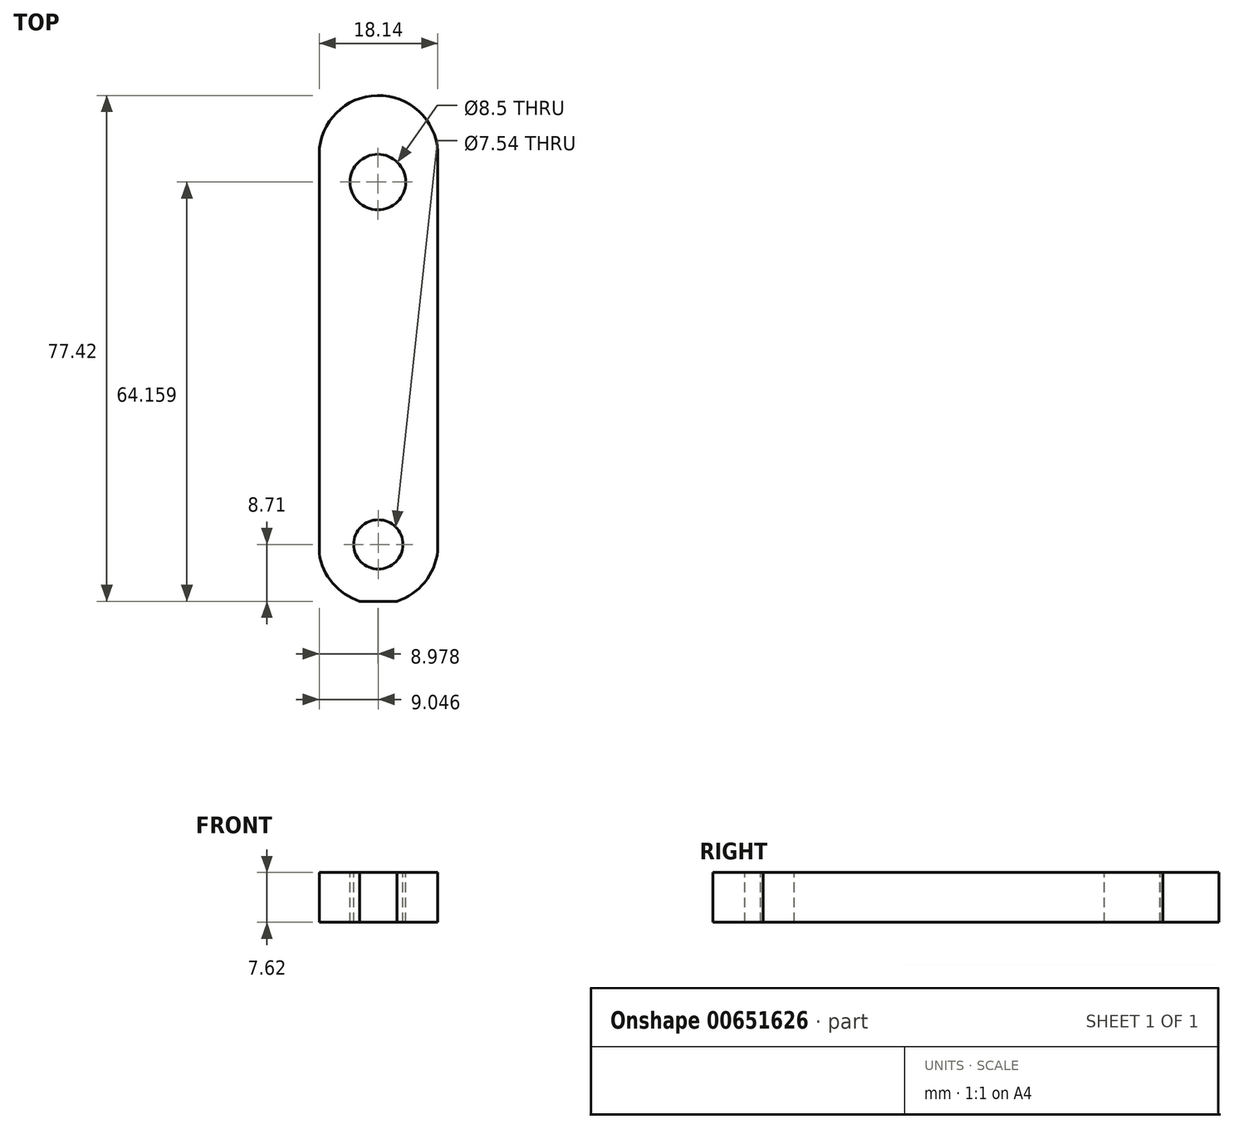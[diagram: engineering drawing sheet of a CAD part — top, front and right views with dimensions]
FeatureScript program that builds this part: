
annotation { "Feature Type Name" : "Feature", "Feature Type Description" : "" }
export const myFeature = defineFeature(function(context is Context, id is Id, definition is map)
    precondition{}
    {
        {
            var Q0;
            Q0=qCreatedBy(makeId("Top.planeOp"),FACE);
            var sketch = newSketch(context, id + "F0", { "sketchPlane" : qUnion([Q0])});
            skLineSegment(sketch, "E0.bottom", {"start": v(-9.26, -43.08) * mm, "end": v(-27.4, -43.08) * mm});
            skLineSegment(sketch, "E0.top", {"start": v(-9.26, 34.64) * mm, "end": v(-27.4, 34.64) * mm});
            skLineSegment(sketch, "E0.left", {"start": v(-9.26, -43.08) * mm, "end": v(-9.26, 34.64) * mm});
            skLineSegment(sketch, "E0.right", {"start": v(-27.4, -43.08) * mm, "end": v(-27.4, 34.64) * mm});
            skSolve(sketch);
        }
        {
            var Q0;
            Q0 = qSketchRegion(id + "F0", true);
            extrude(context, id + "F1", {"entities" : qUnion([Q0]), "depth" : 7.62 * mm, "offsetDistance" : 25.4 * mm});
        }
        {
            var Q0;
            Q0=makeQuery(id+"F1.opExtrude","CAP_FACE",FACE,{"disambiguationData":[OSD([sQuery(id+"F0.wireOp",EDGE,"E0.bottom"),sQuery(id+"F0.wireOp",EDGE,"E0.top"),sQuery(id+"F0.wireOp",EDGE,"E0.left"),sQuery(id+"F0.wireOp",EDGE,"E0.right")])],"isStart":false});
            var sketch = newSketch(context, id + "F2", { "sketchPlane" : qUnion([Q0])});
            skArc(sketch, "E1", {"start": v(-9.26, 24.75) * mm, "mid": v(-18.14, 34.34) * mm, "end": v(-27.4, 25.11) * mm});
            skArc(sketch, "E2", {"start": v(-27.4, -35.74) * mm, "mid": v(-18.17, -43.52) * mm, "end": v(-9.26, -35.38) * mm});
            skSolve(sketch);
        }
        {
            var Q0;
            {var subQ5=makeQuery(id+"F1.opExtrude","CAP_EDGE",EDGE,{"disambiguationData":[OSD([sQuery(id+"F0.wireOp",EDGE,"E0.top")])],"isStart":false});Q0=makeQuery(id+"F2.imprint","IMPRINT",FACE,{"disambiguationData":[TD([[makeQuery(id+"F2.imprint","IMPRINT",EDGE,{"derivedFrom":subQ5}),1.0]])]});}
            var Q1;
            {var subQ0=sQuery(id+"F2.wireOp",EDGE,"E2");var subQ1=makeQuery(id+"F1.opExtrude","CAP_EDGE",EDGE,{"disambiguationData":[OSD([sQuery(id+"F0.wireOp",EDGE,"E0.right")])],"isStart":false});var subQ2=makeQuery(id+"F2.imprint","INTERSECT",VERTEX,{"derivedFrom":[subQ1,subQ0]});Q1=makeQuery(id+"F2.imprint","IMPRINT",FACE,{"disambiguationData":[TD([[makeQuery(id+"F2.imprint","IMPRINT",EDGE,{"disambiguationData":[TD([[subQ2,-1.0]])],"derivedFrom":subQ0}),-1.0]])]});}
            var Q2;
            {var subQ0=sQuery(id+"F2.wireOp",EDGE,"E2");var subQ1=makeQuery(id+"F1.opExtrude","CAP_EDGE",EDGE,{"disambiguationData":[OSD([sQuery(id+"F0.wireOp",EDGE,"E0.left")])],"isStart":false});var subQ2=makeQuery(id+"F2.imprint","INTERSECT",VERTEX,{"derivedFrom":[subQ1,subQ0]});Q2=makeQuery(id+"F2.imprint","IMPRINT",FACE,{"disambiguationData":[TD([[makeQuery(id+"F2.imprint","IMPRINT",EDGE,{"disambiguationData":[TD([[subQ2,1.0]])],"derivedFrom":subQ0}),-1.0]])]});}
            extrude(context, id + "F3", {"entities" : qUnion([Q0, Q1, Q2]), "operationType" : NewBodyOperationType.REMOVE, "oppositeDirection" : true, "depth" : 25.4 * mm, "offsetDistance" : 25.4 * mm});
        }
        {
            var Q0;
            Q0=makeQuery(id+"F1.opExtrude","CAP_FACE",FACE,{"disambiguationData":[OSD([sQuery(id+"F0.wireOp",EDGE,"E0.bottom"),sQuery(id+"F0.wireOp",EDGE,"E0.top"),sQuery(id+"F0.wireOp",EDGE,"E0.left"),sQuery(id+"F0.wireOp",EDGE,"E0.right")])],"isStart":false});
            var sketch = newSketch(context, id + "F4", { "sketchPlane" : qUnion([Q0])});
            skCircle(sketch, "E3", {"center": v(-18.42, 21.08) * mm, "radius": 4.25 * mm});
            skCircle(sketch, "E4", {"center": v(-18.35, -34.37) * mm, "radius": 3.77 * mm});
            skSolve(sketch);
        }
        {
            var Q0;
            Q0=makeQuery(id+"F4.imprint","IMPRINT",FACE,{"disambiguationData":[TD([[makeQuery(id+"F4.imprint","IMPRINT",EDGE,{"derivedFrom":sQuery(id+"F4.wireOp",EDGE,"E4")}),1.0]])]});
            var Q1;
            Q1=makeQuery(id+"F4.imprint","IMPRINT",FACE,{"disambiguationData":[TD([[makeQuery(id+"F4.imprint","IMPRINT",EDGE,{"derivedFrom":sQuery(id+"F4.wireOp",EDGE,"E3")}),1.0]])]});
            extrude(context, id + "F5", {"entities" : qUnion([Q0, Q1]), "operationType" : NewBodyOperationType.REMOVE, "oppositeDirection" : true, "depth" : 25.4 * mm, "offsetDistance" : 25.4 * mm});
        }
    });
